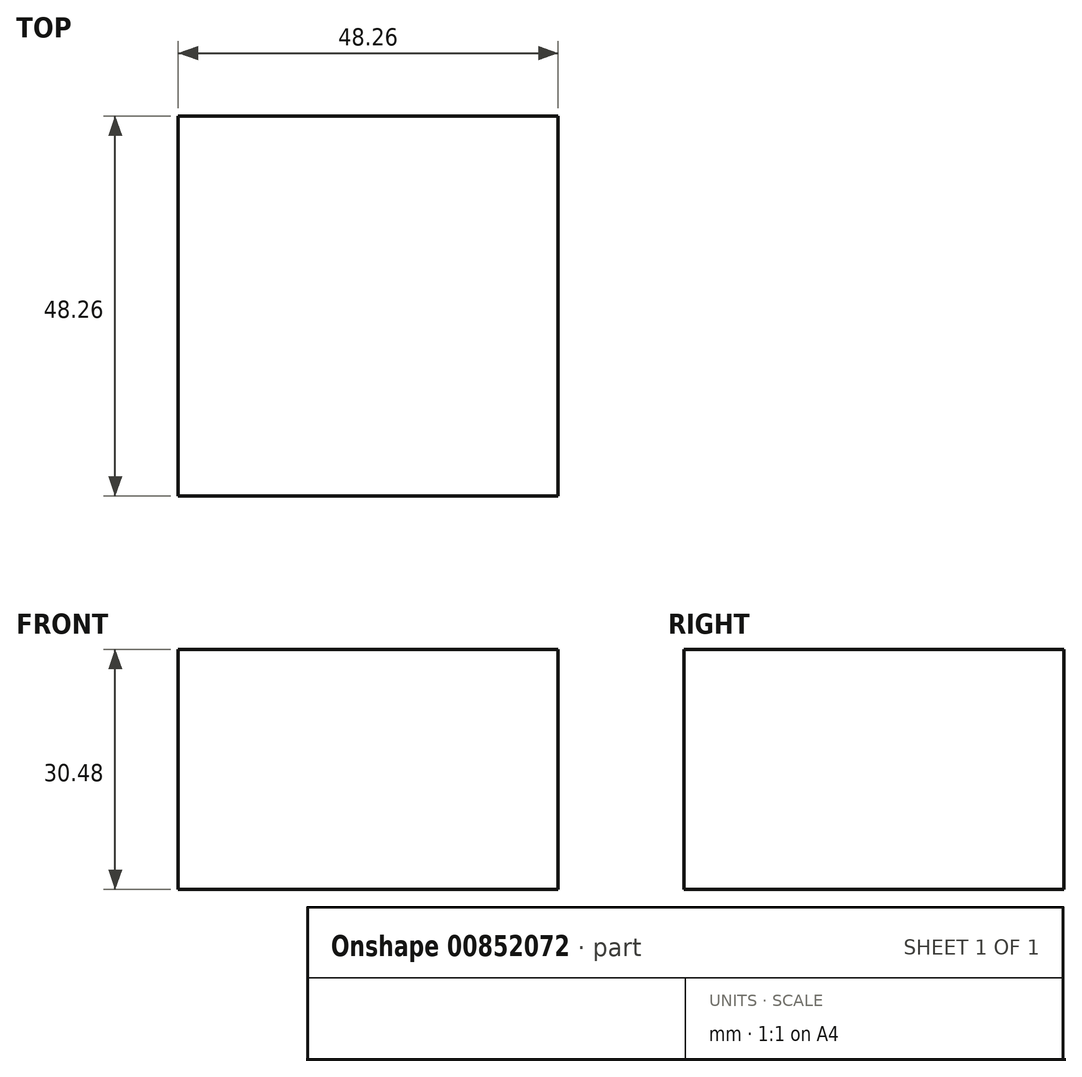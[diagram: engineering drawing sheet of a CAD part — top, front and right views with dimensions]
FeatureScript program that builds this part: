
annotation { "Feature Type Name" : "Feature", "Feature Type Description" : "" }
export const myFeature = defineFeature(function(context is Context, id is Id, definition is map)
    precondition{}
    {
        {
            var Q0;
            Q0=qCreatedBy(makeId("Top.planeOp"),FACE);
            var sketch = newSketch(context, id + "F0", { "sketchPlane" : qUnion([Q0])});
            skLineSegment(sketch, "E0.bottom", {"start": v(-24.13, -24.13) * mm, "end": v(24.13, -24.13) * mm});
            skLineSegment(sketch, "E0.top", {"start": v(-24.13, 24.13) * mm, "end": v(24.13, 24.13) * mm});
            skLineSegment(sketch, "E0.left", {"start": v(-24.13, -24.13) * mm, "end": v(-24.13, 24.13) * mm});
            skLineSegment(sketch, "E0.right", {"start": v(24.13, -24.13) * mm, "end": v(24.13, 24.13) * mm});
            skLineSegment(sketch, "E1", {"start": v(-24.13, 24.13) * mm, "end": v(24.13, -24.13) * mm, "construction": true});
            skSolve(sketch);
        }
        {
            var Q0;
            Q0 = qSketchRegion(id + "F0", true);
            extrude(context, id + "F1", {"entities" : qUnion([Q0]), "depth" : 30.48 * mm, "offsetDistance" : 25.4 * mm});
        }
    });
